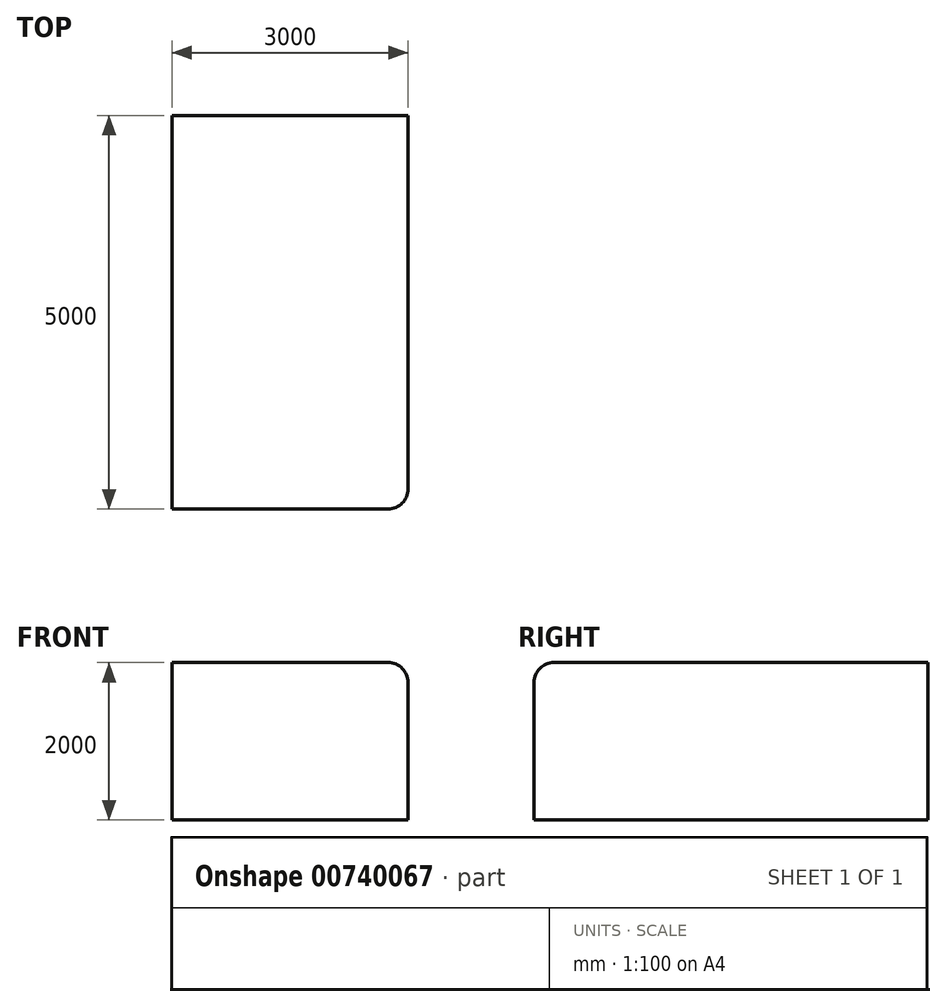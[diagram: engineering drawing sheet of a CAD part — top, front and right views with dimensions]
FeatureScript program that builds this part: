
annotation { "Feature Type Name" : "Feature", "Feature Type Description" : "" }
export const myFeature = defineFeature(function(context is Context, id is Id, definition is map)
    precondition{}
    {
        {
            var Q0;
            Q0=qCreatedBy(makeId("Top.planeOp"),FACE);
            var sketch = newSketch(context, id + "F0", { "sketchPlane" : qUnion([Q0])});
            skLineSegment(sketch, "E0.bottom", {"start": v(1500, 2500) * mm, "end": v(-1500, 2500) * mm});
            skLineSegment(sketch, "E0.top", {"start": v(1500, -2500) * mm, "end": v(-1500, -2500) * mm});
            skLineSegment(sketch, "E0.left", {"start": v(1500, 2500) * mm, "end": v(1500, -2500) * mm});
            skLineSegment(sketch, "E0.right", {"start": v(-1500, 2500) * mm, "end": v(-1500, -2500) * mm});
            skPoint(sketch, "E0.middle", {"position": v(0, 0) * mm});
            skSolve(sketch);
        }
        {
            var Q0;
            Q0 = qSketchRegion(id + "F0", true);
            extrude(context, id + "F1", {"entities" : qUnion([Q0]), "depth" : 2000 * mm, "offsetDistance" : 25.4 * mm});
        }
        {
            var Q0;
            Q0=makeQuery(id+"F1.opExtrude","CAP_EDGE",EDGE,{"disambiguationData":[OSD([sQuery(id+"F0.wireOp",EDGE,"E0.top")])],"isStart":false});
            fillet(context, id + "F2", {"entities" : qUnion([Q0]), "radius" : 254 * mm, "tangentPropagation" : true, "allowEdgeOverflow" : false});
        }
        {
            var Q0;
            Q0=makeQuery(id+"F1.opExtrude","SWEPT_EDGE",EDGE,{"disambiguationData":[OSD([sQuery(id+"F0.wireOp",EDGE,"E0.top"),sQuery(id+"F0.wireOp",EDGE,"E0.left")])]});
            var Q1;
            Q1=makeQuery(id+"F2.opFillet","BLEND_EDGE",EDGE,{"blendedFrom":[makeQuery(id+"F1.opExtrude","CAP_EDGE",EDGE,{"disambiguationData":[OSD([sQuery(id+"F0.wireOp",EDGE,"E0.top")])],"isStart":false}),makeQuery(id+"F1.opExtrude","SWEPT_FACE",FACE,{"disambiguationData":[OSD([sQuery(id+"F0.wireOp",EDGE,"E0.left")])]})],"blendedInto":[makeQuery(id+"F1.opExtrude","SWEPT_FACE",FACE,{"disambiguationData":[OSD([sQuery(id+"F0.wireOp",EDGE,"E0.left")])]})]});
            var Q2;
            Q2=makeQuery(id+"F1.opExtrude","CAP_EDGE",EDGE,{"disambiguationData":[OSD([sQuery(id+"F0.wireOp",EDGE,"E0.left")])],"isStart":false});
            fillet(context, id + "F3", {"entities" : qUnion([Q0, Q1, Q2]), "radius" : 254 * mm, "tangentPropagation" : true, "allowEdgeOverflow" : false});
        }
    });
